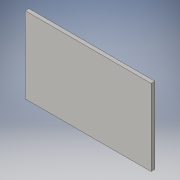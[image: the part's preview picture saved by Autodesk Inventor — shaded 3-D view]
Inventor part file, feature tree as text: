
AUTODESK INVENTOR PART (.ipt)
format: ipt  version: 2016 (Build 200138000, 138)  size: 86,528 bytes
history: native  units: in
note: dims shown in document units (in); Inventor stores cm internally (conversion verified against a paired STEP export)
features: extrude x1, sketch x1
ambient origin geometry x8: Origin, YZ Plane, XZ Plane, XY Plane, X Axis, Y Axis, Z Axis, Center Point
bodies: Solid1 (feature_tree)
feature tree (2):
  extrude  "Extrusion1"  Depth=10.0in
  sketch  "Sketch1"  dims[d0=16.5in d1=10.0in d2=0.5in d3=0.0in]
